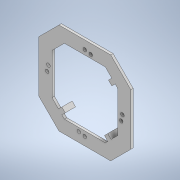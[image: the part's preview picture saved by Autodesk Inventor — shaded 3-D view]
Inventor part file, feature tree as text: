
AUTODESK INVENTOR PART (.ipt)
format: ipt  version: 2021.2 (Build 252289000, 289)  size: 198,656 bytes
history: native  units: mm
features: extrude x3, sketch x3, other x3, reference x1, projected_geometry x1
ambient origin geometry x8: Origin, YZ Plane, XZ Plane, XY Plane, X Axis, Y Axis, Z Axis, Center Point
bodies: Body1 (feature_tree)
feature tree (11):
  extrude  "Выдавливание2"  Depth=11.0mm
  sketch  "Эскиз2"
  other  "РабПлоскость1"
  extrude  "Выдавливание3"  Depth=11.0mm
  extrude  "Выдавливание4"  Depth=3.0mm
  sketch  "Эскиз1"
  reference  "Ссылка1"
  projected_geometry  "Спроецированная петля1"
  sketch  "Эскиз3"
  other  "Сборка1"
  other  "Низ:1"
